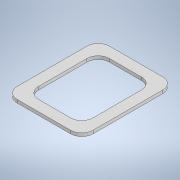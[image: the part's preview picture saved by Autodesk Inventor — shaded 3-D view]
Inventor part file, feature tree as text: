
AUTODESK INVENTOR PART (.ipt)
format: ipt  version: 2020 (Build 240168000, 168)  size: 131,072 bytes
history: native  units: in
note: dims shown in document units (in); Inventor stores cm internally (conversion verified against a paired STEP export)
features: fillet x2, extrude x1, sketch x1
ambient origin geometry x8: Origin, YZ Plane, XZ Plane, XY Plane, X Axis, Y Axis, Z Axis, Center Point
bodies: Solid1 (feature_tree)
feature tree (4):
  extrude  "Extrusion1"  Depth=0.4165in
  fillet  "Fillet1"  Radius=1.7795in
  fillet  "Fillet2"  Radius=2.3858in
  sketch  "Sketch1"  dims[d0=0.5118in d1=0.5118in d2=1.7795in d3=2.3858in d4=0.5118in d5=0.5118in d6=0.1181in d7=0.1181in d8=0.1181in d9=0.1181in d10=0.1181in d11=0.0in d12=0.4165in d13=0.4165in]
